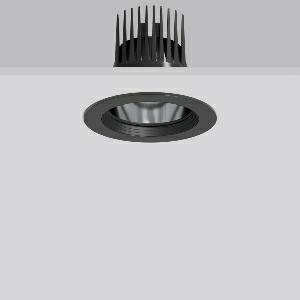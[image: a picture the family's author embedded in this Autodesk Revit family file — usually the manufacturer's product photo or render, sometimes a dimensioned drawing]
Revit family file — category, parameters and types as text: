
# Revit family: heledon_maxi_e_901759_003_3_76_c0d8
name_source: partatom
category: Lighting Fixtures
units: mm (PartAtom-declared; Revit-internal decimal feet)

## family parameters
Cut with Voids When Loaded = No
Host = Face
Light Source = No
Part Type = Normal
Room Calculation Point = No
Round Connector Dimension = Use Diameter
Shared = No

## types (1)
- HELEDON maxi E (1 x LED Modul 935, 3250 lm, 3500)
    Apparent Load = 25 VA
    Approval mark = CE
    CIE Flux Codes = 97 100 100 100 100
    Color Rendering = 92
    Color Temperature = 3500
    Default Elevation = 1800 mm
    Description = Series: HELEDON maxi
Round recessed downlight. Housing: die-cast aluminium, powder-coated. Black plastic ring and recessed LED to prevent glare from the side. Optical assembly with reflector made of MIRO-Silver with 98% total light reflection for outstanding efficiency - can be changed without tools. Best colour rendering index Ra>90. Suitable for Recessed ceiling mounting. Installation without tools thanks to spring fastening system. Including separate LED converter with connecting cable 600 mm.High quality converter without flickering and stroboscopic effect. Through-wiring box (5 pole) available as accessory. The following accessories can be mounted without use of tools: interchangeable lenses, decorative glasses, honeycomb louvre, clear and frosted diffusers, white interchangeable plastic ring. 
Colour: deep black, matt (RAL 9005)
Diameter: 162 mm
Height: 3 mm
Cut-out diameter: 152 mm
Recess height: 200 mm
Luminaire: recess height: 135 mm
Lamp: LED
Socket: without socket
Colour temperature: 3500K
Colour rendering index (CRI): 92
System power: 25 W
Rated luminous flux: 3250 lm
Luminous efficiency: 130 lm/W
Control gear: Converter, dimmable, DALI
Protection class: II
Type of protection: IP 20
    Height = 0 mm  [stored 0 ft]
    Lamp = 1 x LED Modul 935
    Lamp Light Flux = 3250 lm
    Lamp count = 1
    Length = 162 mm
    Lifetime = 50000 h
    Luminous efficacy = 130 lm/W
    Manufacturer = RZB
    ModVariant = No
    Model = 901759.003.3.76
    Mounting Place = Ceiling
    Mounting Type = Recessed
    Number of Poles = 1
    OnlyDefault = Yes
    Power Factor = 1
    Product Name = HELEDON maxi E
    Product group = Recessed downlights
    ProductGroupID = 402
    Protection Class = Protection class II
    Protection Degree = IP 20
    RLX_Detail_Level = 1
    RLX_Emergency_Light_Flux = 0 lm
    RLX_Emergency_Type = 0
    RLX_Emergency_Type_DB = No
    RlxData = <blob elided: 120481 chars, md5=437a812a>
    Socket = socket
    Standby Power = 0 W
    System Light Flux = 3250 lm
    System Power = 25 W
    Type Comments = Product without accessories
    Type Image = 901662.003.jpg
    URL = http://relux.com
    VarID = ---
    Voltage = 230 V
    Voltage Range = 220-240 V
    Weight = 0.00 kg
    Width = 0 mm  [stored 0 ft]

note: [stored X ft] marks values corroborated as IEEE doubles in the binary element streams (Revit-internal decimal feet)

## geometry (parser evidence)
native form markers: Blend x4, Sweep x11
no freeform markers — native parametric forms only
